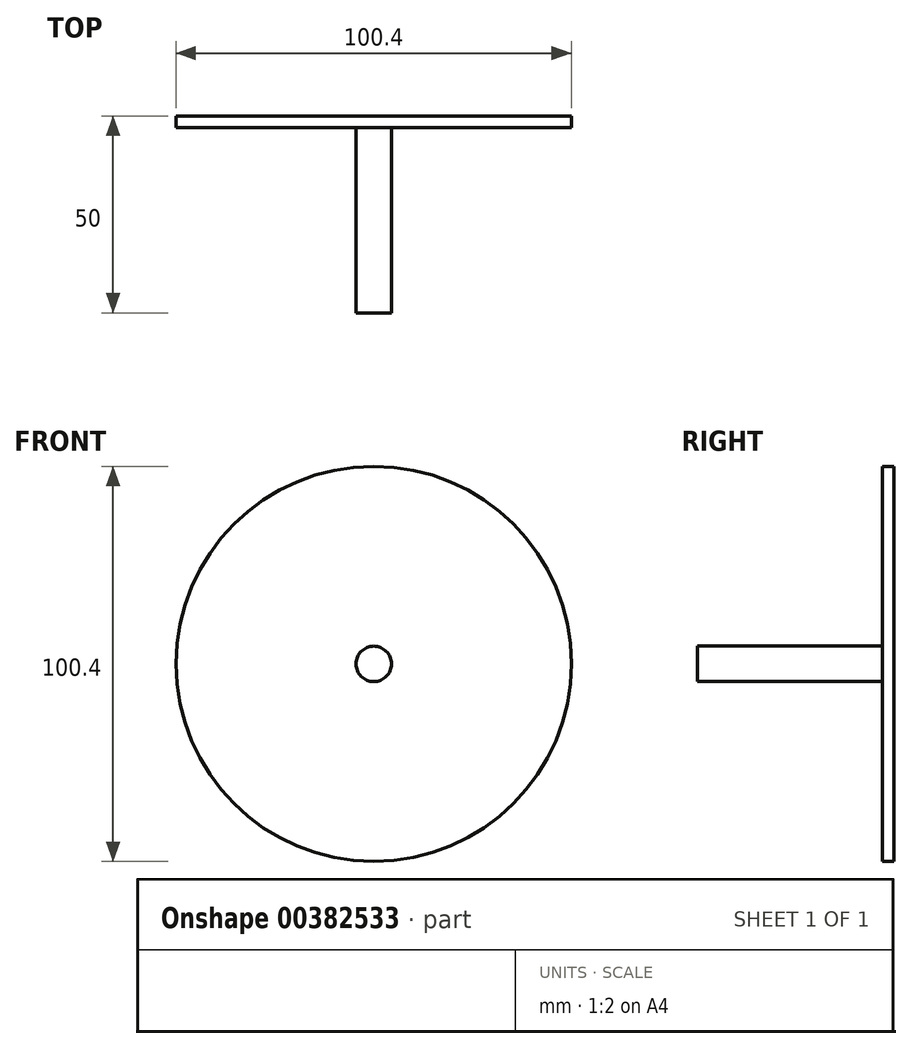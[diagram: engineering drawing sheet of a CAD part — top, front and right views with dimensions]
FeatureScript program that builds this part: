
annotation { "Feature Type Name" : "Feature", "Feature Type Description" : "" }
export const myFeature = defineFeature(function(context is Context, id is Id, definition is map)
    precondition{}
    {
        {
            var Q0;
            Q0=qCreatedBy(makeId("Front.planeOp"),FACE);
            var sketch = newSketch(context, id + "F0", { "sketchPlane" : qUnion([Q0])});
            skCircle(sketch, "E0", {"center": v(0, 0) * mm, "radius": 50.2 * mm});
            skCircle(sketch, "E1", {"center": v(0, 0) * mm, "radius": 4.5 * mm});
            skSolve(sketch);
        }
        {
            var Q0;
            Q0 = qSketchRegion(id + "F0", true);
            extrude(context, id + "F1", {"entities" : qUnion([Q0]), "depth" : 3 * mm});
        }
        {
            var Q0;
            Q0=qCreatedBy(makeId("Front.planeOp"),FACE);
            var sketch = newSketch(context, id + "F2", { "sketchPlane" : qUnion([Q0])});
            skCircle(sketch, "E2", {"center": v(0, 0) * mm, "radius": 7.13 * mm});
            skSolve(sketch);
        }
        {
            var Q0;
            Q0=sQuery(id+"F2.wireOp",EDGE,"E2");
            extrude(context, id + "F3", {"bodyType" : ToolBodyType.SURFACE, "surfaceEntities" : qUnion([Q0]), "depth" : 3 * mm});
        }
        {
            var Q0;
            Q0=qCreatedBy(makeId("Front.planeOp"),FACE);
            var sketch = newSketch(context, id + "F4", { "sketchPlane" : qUnion([Q0])});
            skCircle(sketch, "E3", {"center": v(0, 0) * mm, "radius": 4.5 * mm});
            skSolve(sketch);
        }
        {
            var Q0;
            Q0=makeQuery(id+"F4.imprint","IMPRINT",FACE,{"disambiguationData":[TD([[makeQuery(id+"F4.imprint","IMPRINT",EDGE,{"derivedFrom":sQuery(id+"F4.wireOp",EDGE,"E3")}),1.0]])]});
            extrude(context, id + "F5", {"entities" : qUnion([Q0]), "operationType" : NewBodyOperationType.ADD, "depth" : 50 * mm});
        }
    });
